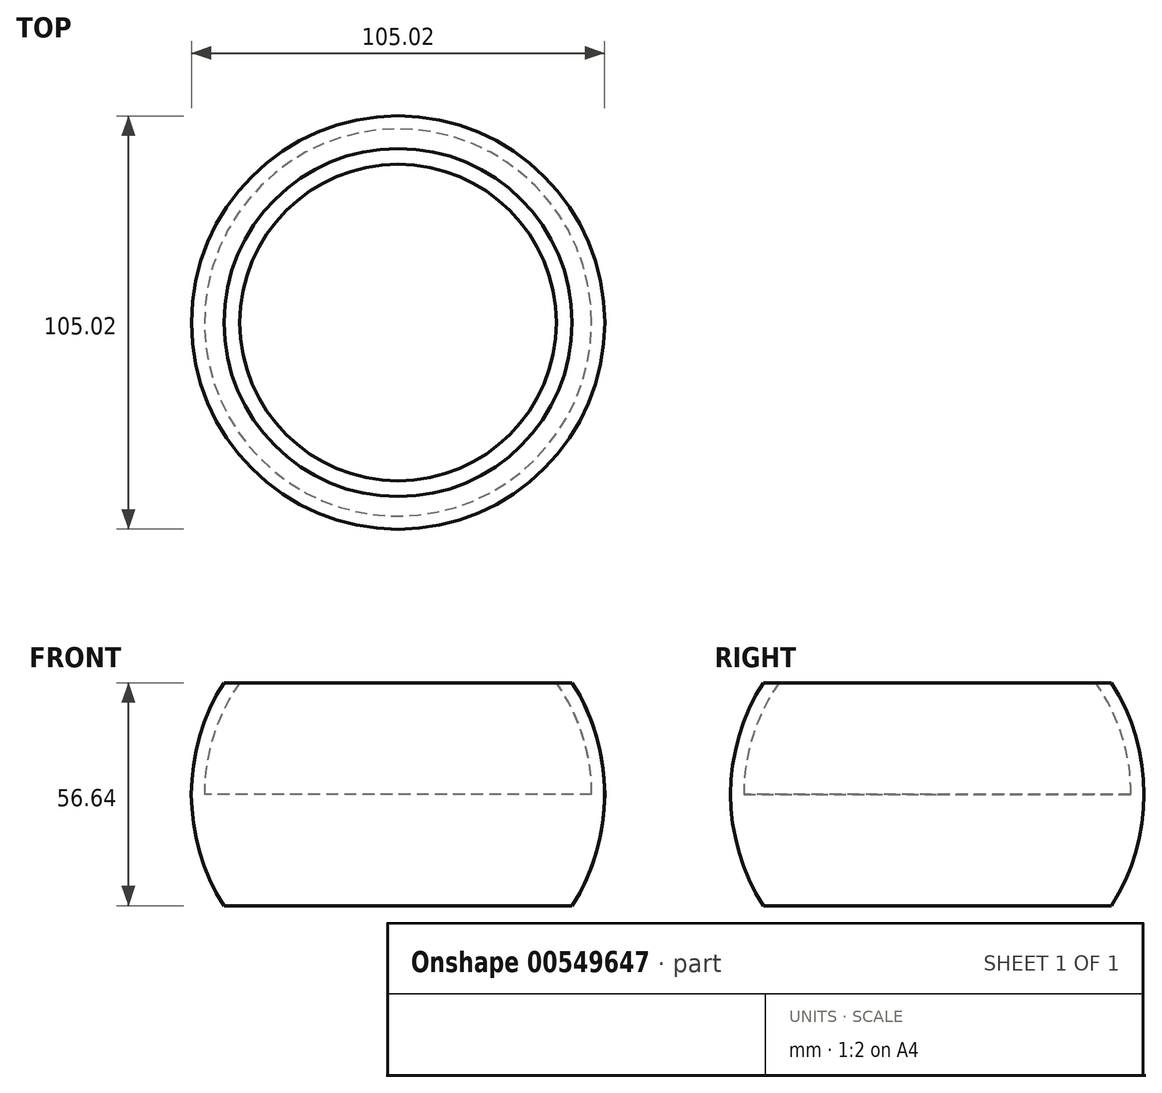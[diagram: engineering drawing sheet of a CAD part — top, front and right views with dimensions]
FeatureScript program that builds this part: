
annotation { "Feature Type Name" : "Feature", "Feature Type Description" : "" }
export const myFeature = defineFeature(function(context is Context, id is Id, definition is map)
    precondition{}
    {
        {
            var Q0;
            Q0=qCreatedBy(makeId("Front.planeOp"),FACE);
            var sketch = newSketch(context, id + "F0", { "sketchPlane" : qUnion([Q0])});
            skLineSegment(sketch, "E0", {"start": v(40.21, 28.32) * mm, "end": v(44.22, 28.32) * mm});
            skLineSegment(sketch, "E1.MirrorCS", {"start": v(0, -28.32) * mm, "end": v(44.22, -28.32) * mm});
            skLineSegment(sketch, "E2", {"start": v(0, 0) * mm, "end": v(0, -28.32) * mm});
            skArc(sketch, "E3.trimOffspring", {"start": v(44.22, -28.32) * mm, "mid": v(52.51, 0) * mm, "end": v(44.22, 28.32) * mm});
            skPoint(sketch, "E4.orphan", {"position": v(-52.51, 0) * mm});
            skPoint(sketch, "E5.orphan", {"position": v(-44.22, 28.32) * mm});
            skPoint(sketch, "E6.orphan", {"position": v(-44.22, -28.32) * mm});
            skArc(sketch, "E7", {"start": v(49.19, 0) * mm, "mid": v(46.9, 14.86) * mm, "end": v(40.21, 28.32) * mm});
            skLineSegment(sketch, "E8", {"start": v(0, 0) * mm, "end": v(49.19, 0) * mm});
            skPoint(sketch, "E9.orphan", {"position": v(0, 28.32) * mm});
            skLineSegment(sketch, "E10", {"start": v(40.21, 28.32) * mm, "end": v(21.2, 0) * mm});
            skLineSegment(sketch, "E11", {"start": v(21.2, 0) * mm, "end": v(0, 0) * mm});
            skLineSegment(sketch, "E12", {"start": v(0, 10.86) * mm, "end": v(15.47, 10.86) * mm});
            skLineSegment(sketch, "E13", {"start": v(15.47, 10.86) * mm, "end": v(35.96, 28.32) * mm});
            skLineSegment(sketch, "E14", {"start": v(35.96, 28.32) * mm, "end": v(40.21, 28.32) * mm});
            skFitSpline(sketch, "E15", {"points": [v(15.47, 10.86) * mm, v(5.8, 13.82) * mm, v(0, 14.23) * mm], "startDerivative": vector(-18.01, 6.41) * mm, "endDerivative": vector(-12.67, 0.03) * mm});
            skLineSegment(sketch, "E16", {"start": v(0, 14.23) * mm, "end": v(0, 10.86) * mm});
            skLineSegment(sketch, "E17", {"start": v(0, 10.86) * mm, "end": v(0, 0) * mm});
            skSolve(sketch);
        }
        {
            var Q0;
            Q0=makeQuery(id+"F0.imprint","IMPRINT",FACE,{"disambiguationData":[TD([[makeQuery(id+"F0.imprint","IMPRINT",EDGE,{"derivedFrom":sQuery(id+"F0.wireOp",EDGE,"E0")}),-1.0]])]});
            var Q1;
            Q1=sQuery(id+"F0.wireOp",EDGE,"E2");
            revolve(context, id + "F1", {"entities" : qUnion([Q0]), "axis" : qUnion([Q1]), "revolveType" : RevolveType.FULL});
        }
    });
